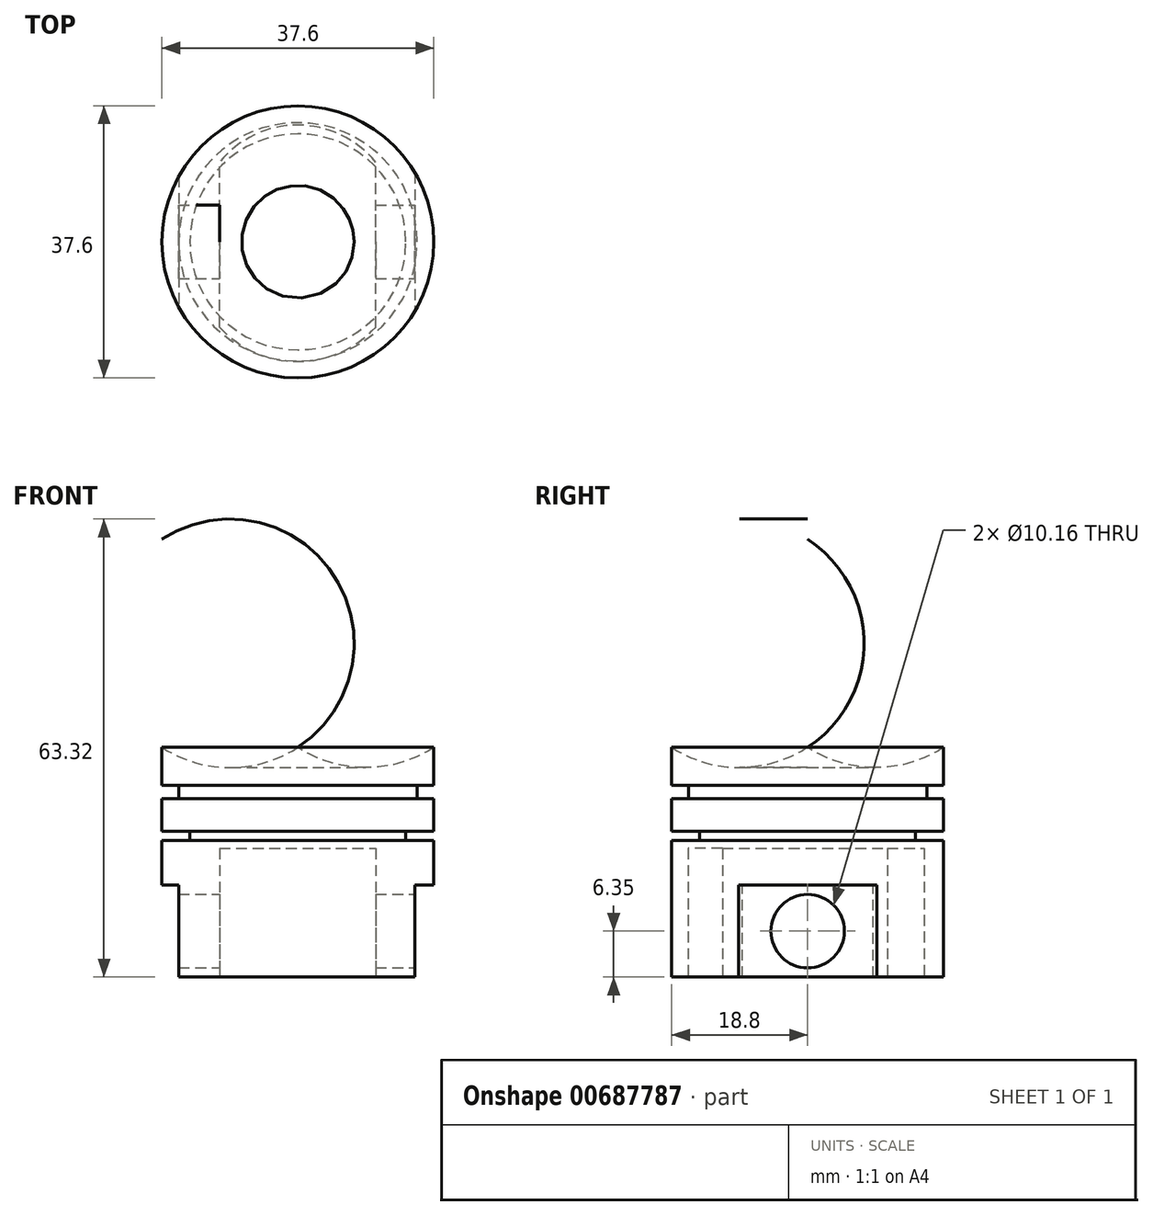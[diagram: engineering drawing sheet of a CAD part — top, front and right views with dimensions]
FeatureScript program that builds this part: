
annotation { "Feature Type Name" : "Feature", "Feature Type Description" : "" }
export const myFeature = defineFeature(function(context is Context, id is Id, definition is map)
    precondition{}
    {
        {
            var Q0;
            Q0=qCreatedBy(makeId("Front.planeOp"),FACE);
            var sketch = newSketch(context, id + "F0", { "sketchPlane" : qUnion([Q0])});
            skLineSegment(sketch, "E0", {"start": v(0, 0) * mm, "end": v(0, 19.05) * mm});
            skLineSegment(sketch, "E1", {"start": v(0, 0) * mm, "end": v(18.8, 0) * mm});
            skLineSegment(sketch, "E2", {"start": v(18.8, 0) * mm, "end": v(18.8, 6.19) * mm});
            skArc(sketch, "E3", {"start": v(0, 19.05) * mm, "mid": v(9.4, 16.25) * mm, "end": v(18.8, 19.05) * mm});
            skLineSegment(sketch, "E4.bottom", {"start": v(18.8, 13.8) * mm, "end": v(16.48, 13.8) * mm});
            skLineSegment(sketch, "E4.top", {"start": v(18.8, 11.97) * mm, "end": v(16.48, 11.97) * mm});
            skLineSegment(sketch, "E4.right", {"start": v(16.48, 13.8) * mm, "end": v(16.48, 11.97) * mm});
            skLineSegment(sketch, "E5.bottom", {"start": v(18.8, 7.46) * mm, "end": v(14.93, 7.46) * mm});
            skLineSegment(sketch, "E5.top", {"start": v(18.8, 6.19) * mm, "end": v(14.93, 6.19) * mm});
            skLineSegment(sketch, "E5.right", {"start": v(14.93, 7.46) * mm, "end": v(14.93, 6.19) * mm});
            skLineSegment(sketch, "E6.trimOffspring", {"start": v(18.8, 13.8) * mm, "end": v(18.8, 19.05) * mm});
            skLineSegment(sketch, "E7.trimOffspring", {"start": v(18.8, 7.46) * mm, "end": v(18.8, 11.97) * mm});
            skSolve(sketch);
        }
        {
            var Q0;
            Q0 = qSketchRegion(id + "F0", true);
            var Q1;
            Q1=sQuery(id+"F0.wireOp",EDGE,"E0");
            revolve(context, id + "F1", {"entities" : qUnion([Q0]), "axis" : qUnion([Q1]), "revolveType" : RevolveType.FULL});
        }
        {
            var Q0;
            Q0=makeQuery(id+"F1.opRevolve","SWEPT_FACE",FACE,{"disambiguationData":[OSD([sQuery(id+"F0.wireOp",EDGE,"E1")])]});
            var sketch = newSketch(context, id + "F2", { "sketchPlane" : qUnion([Q0])});
            skLineSegment(sketch, "E8", {"start": v(-16.47, -9.56) * mm, "end": v(-16.47, 9.05) * mm});
            skLineSegment(sketch, "E9", {"start": v(16.18, -9.56) * mm, "end": v(16.18, 10.05) * mm});
            skSolve(sketch);
        }
        {
            var Q0;
            Q0 = qSketchRegion(id + "F2", true);
            var Q1;
            {var subQ0=sQuery(id+"F2.wireOp",EDGE,"E8");var subQ1=makeQuery(id+"F1.opRevolve","SWEPT_EDGE",EDGE,{"disambiguationData":[OSD([sQuery(id+"F0.wireOp",EDGE,"E1"),sQuery(id+"F0.wireOp",EDGE,"E2")])]});var subQ2=makeQuery(id+"F2.imprint","INTERSECT",VERTEX,{"disambiguationData":[OD(0.0)],"derivedFrom":[subQ1,subQ0]});Q1=makeQuery(id+"F2.imprint","IMPRINT",FACE,{"disambiguationData":[TD([[makeQuery(id+"F2.imprint","IMPRINT",EDGE,{"disambiguationData":[TD([[subQ2,1.0]])],"derivedFrom":subQ0}),-1.0]])]});}
            extrude(context, id + "F3", {"entities" : qUnion([Q0, Q1]), "operationType" : NewBodyOperationType.ADD, "depth" : 12.7 * mm, "offsetDistance" : 25.4 * mm});
        }
        {
            var Q0;
            Q0=makeQuery(id+"F3.opExtrude","CAP_FACE",FACE,{"disambiguationData":[OSD([sQuery(id+"F0.wireOp",EDGE,"E1"),sQuery(id+"F0.wireOp",EDGE,"E2"),sQuery(id+"F2.wireOp",EDGE,"E8"),sQuery(id+"F2.wireOp",EDGE,"E9")])],"isStart":false});
            var sketch = newSketch(context, id + "F4", { "sketchPlane" : qUnion([Q0])});
            skLineSegment(sketch, "E10", {"start": v(-10.84, 11.8) * mm, "end": v(-10.84, -11.01) * mm});
            skLineSegment(sketch, "E11", {"start": v(10.76, 11.8) * mm, "end": v(10.76, -11.01) * mm});
            skArc(sketch, "E12", {"start": v(-10.84, -11.01) * mm, "mid": v(-0.04, -16.13) * mm, "end": v(10.76, -11.01) * mm});
            skArc(sketch, "E13", {"start": v(10.76, 11.8) * mm, "mid": v(-0.04, 16.53) * mm, "end": v(-10.84, 11.8) * mm});
            skSolve(sketch);
        }
        {
            var Q0;
            Q0=makeQuery(id+"F4.imprint","IMPRINT",FACE,{"disambiguationData":[TD([[makeQuery(id+"F4.imprint","IMPRINT",EDGE,{"derivedFrom":sQuery(id+"F4.wireOp",EDGE,"E10")}),1.0]])]});
            extrude(context, id + "F5", {"entities" : qUnion([Q0]), "operationType" : NewBodyOperationType.REMOVE, "oppositeDirection" : true, "depth" : 17.78 * mm, "offsetDistance" : 25.4 * mm});
        }
        {
            var Q0;
            Q0=makeQuery(id+"F3.opExtrude","SWEPT_FACE",FACE,{"disambiguationData":[OSD([sQuery(id+"F2.wireOp",EDGE,"E9")])]});
            var sketch = newSketch(context, id + "F6", { "sketchPlane" : qUnion([Q0])});
            skCircle(sketch, "E14", {"center": v(0, -6.35) * mm, "radius": 5.08 * mm});
            skPoint(sketch, "E14.centerSnap0", {"position": v(-9.56, -6.35) * mm});
            skSolve(sketch);
        }
        {
            var Q0;
            Q0=makeQuery(id+"F6.imprint","IMPRINT",FACE,{"disambiguationData":[TD([[makeQuery(id+"F6.imprint","IMPRINT",EDGE,{"derivedFrom":sQuery(id+"F6.wireOp",EDGE,"E14")}),1.0]])]});
            extrude(context, id + "F7", {"entities" : qUnion([Q0]), "operationType" : NewBodyOperationType.REMOVE, "oppositeDirection" : true, "depth" : 127 * mm, "offsetDistance" : 25.4 * mm});
        }
    });
